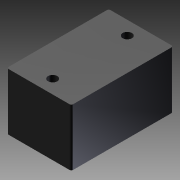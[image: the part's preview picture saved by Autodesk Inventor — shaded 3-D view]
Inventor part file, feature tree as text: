
AUTODESK INVENTOR PART (.ipt)
format: ipt  version: 2011 SP1 (Build 150282100, 282)  size: 140,800 bytes
history: native  units: in
note: dims shown in document units (in); Inventor stores cm internally (conversion verified against a paired STEP export)
features: other x35, sketch x7, extrude x5, hole x2
ambient origin geometry x8: Origin, YZ Plane, XZ Plane, XY Plane, X Axis, Y Axis, Z Axis, Center Point
bodies: Solid1 (feature_tree)
feature tree (49):
  extrude  "Extrusion1"  Depth=0.01in TaperAngle=0.0deg
  extrude  "Extrusion2"  Depth=0.01in TaperAngle=0.0deg
  extrude  "Extrusion3"  [1 undecoded]
  extrude  "Extrusion4"  [1 undecoded]
  extrude  "Extrusion5"  [1 undecoded]
  hole  "Drilling 1"  [1 undecoded]
  hole  "Drilling 2"  [1 undecoded]
  other  "screw_m25_2_XY"
  other  "screw_m25_2_YZ"
  other  "screw_m25_2_ZX"
  other  "screw_m25_2_X"
  other  "screw_m25_2_Y"
  other  "screw_m25_2_Z"
  other  "screw_m25_2_Center"
  other  "sscrew_m25_1_XY"
  other  "sscrew_m25_1_YZ"
  other  "sscrew_m25_1_ZX"
  other  "sscrew_m25_1_X"
  other  "sscrew_m25_1_Y"
  other  "sscrew_m25_1_Z"
  other  "sscrew_m25_1_Center"
  other  "to_dummy_XY"
  other  "to_dummy_YZ"
  other  "to_dummy_ZX"
  other  "to_dummy_X"
  other  "to_dummy_Y"
  other  "to_dummy_Z"
  other  "to_dummy_Center"
  other  "to_electric_XY"
  other  "to_electric_YZ"
  other  "to_electric_ZX"
  other  "to_electric_X"
  other  "to_electric_Y"
  other  "to_electric_Z"
  other  "to_electric_Center"
  other  "to_panel_XY"
  other  "to_panel_YZ"
  other  "to_panel_ZX"
  other  "to_panel_X"
  other  "to_panel_Y"
  other  "to_panel_Z"
  other  "to_panel_Center"
  sketch  "Sketch_1"  dims[d0=0.61in d1=0.0in d2=0.01in d3=0.0in]
  sketch  "Sketch_2"  dims[d4=0.01in d5=0.0in d6=0.01in d7=0.0in]
  sketch  "Sketch_3"  dims[d8=0.01in d9=0.0in]
  sketch  "Sketch_4"  dims[d10=0.0984in d11=0.75in d12=0.2in d13=0.08in d14=0.5635in d15=0.61in d16=0.0in]
  sketch  "Sketch_5"  dims[d17=0.0984in d18=0.75in d19=0.2in d20=0.08in d21=0.5635in d22=0.61in d23=0.0in]
  sketch  "Sketch6"
  sketch  "Sketch7"
note: 5 required parameter values undecoded (feature->parameter linkage not recoverable at this tier; creation-order binding heuristic only, values carry confidence <= 0.55)
